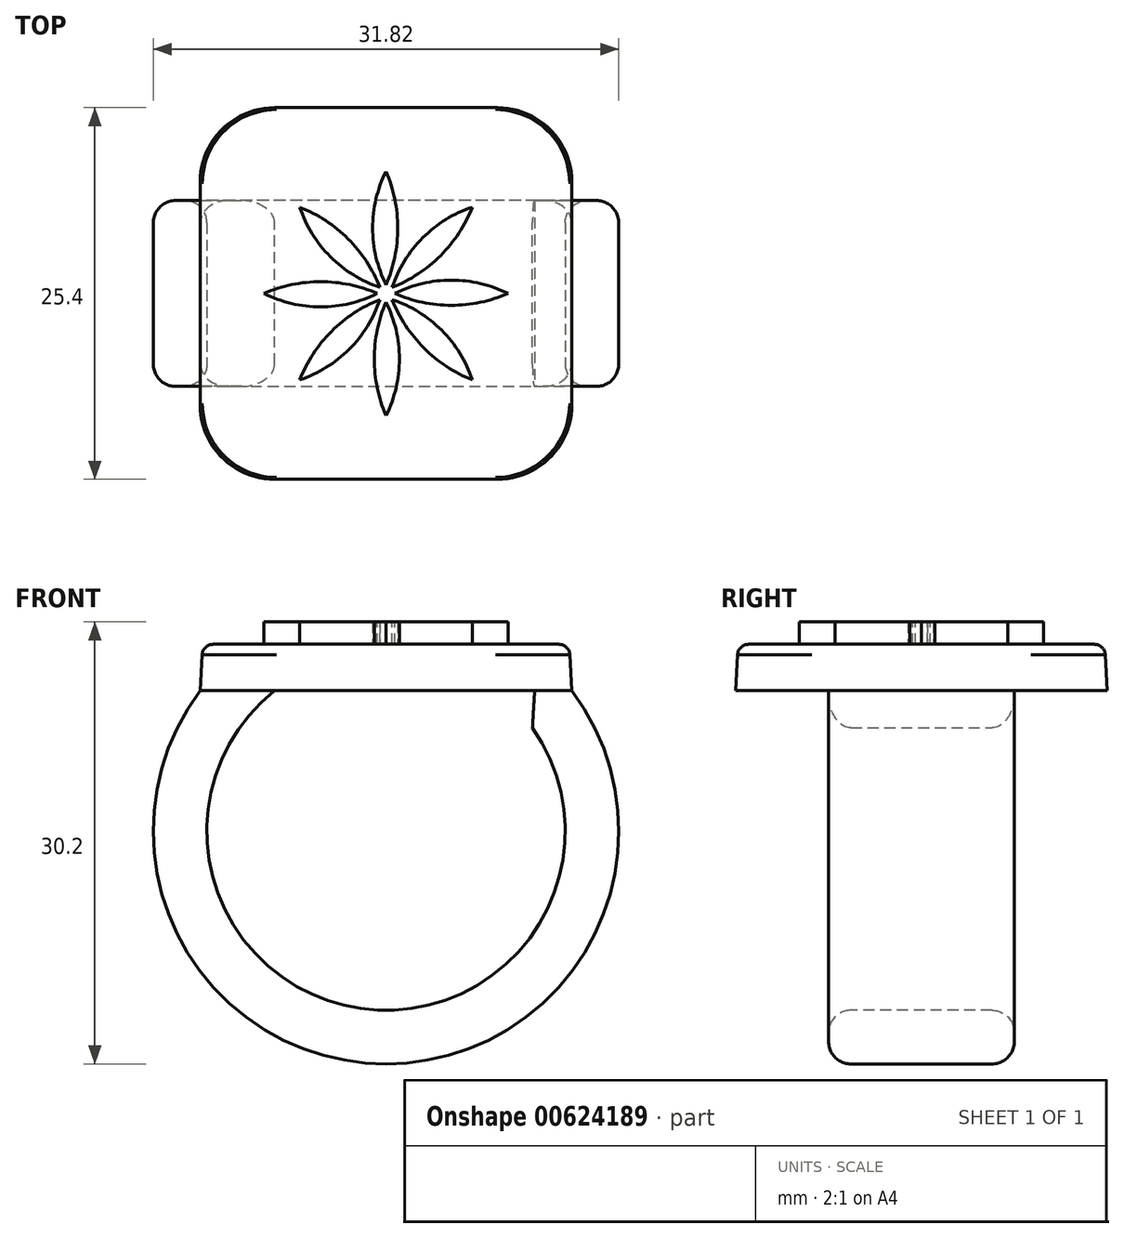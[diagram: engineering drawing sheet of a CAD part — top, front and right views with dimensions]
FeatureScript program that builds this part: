
annotation { "Feature Type Name" : "Feature", "Feature Type Description" : "" }
export const myFeature = defineFeature(function(context is Context, id is Id, definition is map)
    precondition{}
    {
        {
            var Q0;
            Q0=qCreatedBy(makeId("Top.planeOp"),FACE);
            var sketch = newSketch(context, id + "F0", { "sketchPlane" : qUnion([Q0])});
            skLineSegment(sketch, "E0.bottom", {"start": v(12.7, 12.7) * mm, "end": v(-12.7, 12.7) * mm});
            skLineSegment(sketch, "E0.top", {"start": v(12.7, -12.7) * mm, "end": v(-12.7, -12.7) * mm});
            skLineSegment(sketch, "E0.left", {"start": v(12.7, 12.7) * mm, "end": v(12.7, -12.7) * mm});
            skLineSegment(sketch, "E0.right", {"start": v(-12.7, 12.7) * mm, "end": v(-12.7, -12.7) * mm});
            skPoint(sketch, "E0.middle", {"position": v(0, 0) * mm});
            skSolve(sketch);
        }
        {
            var Q0;
            Q0=qSketchRegion(id+"F0",true);
            extrude(context, id + "F1", {"entities" : qUnion([Q0]), "depth" : 3.17 * mm, "hasDraft" : true, "draftAngle" : 3 * degree, "draftPullDirection" : true});
        }
        {
            var Q0;
            Q0=qCreatedBy(makeId("Front.planeOp"),FACE);
            var sketch = newSketch(context, id + "F2", { "sketchPlane" : qUnion([Q0])});
            skArc(sketch, "E1", {"start": v(-10.16, 0) * mm, "mid": v(0, -23.56) * mm, "end": v(10.16, 0) * mm});
            skSolve(sketch);
        }
        {
            var Q0;
            Q0=makeQuery(id+"F1.opExtrude","CAP_FACE",FACE,{"disambiguationData":[OSD([sQuery(id+"F0.wireOp",EDGE,"E0.bottom"),sQuery(id+"F0.wireOp",EDGE,"E0.top"),sQuery(id+"F0.wireOp",EDGE,"E0.left"),sQuery(id+"F0.wireOp",EDGE,"E0.right")])],"isStart":true});
            var sketch = newSketch(context, id + "F3", { "sketchPlane" : qUnion([Q0])});
            skLineSegment(sketch, "E2.bottom", {"start": v(-12.7, 6.35) * mm, "end": v(-7.62, 6.35) * mm});
            skLineSegment(sketch, "E2.top", {"start": v(-12.7, -6.35) * mm, "end": v(-7.62, -6.35) * mm});
            skLineSegment(sketch, "E2.left", {"start": v(-12.7, 6.35) * mm, "end": v(-12.7, -6.35) * mm});
            skLineSegment(sketch, "E2.right", {"start": v(-7.62, 6.35) * mm, "end": v(-7.62, -6.35) * mm});
            skPoint(sketch, "E2.middle", {"position": v(-10.16, 0) * mm});
            skSolve(sketch);
        }
        {
            var Q0;
            Q0=qSketchRegion(id+"F3",true);
            var Q1;
            Q1=qConstructionFilter(qBodyType(qCreatedBy(id+"F2",EDGE),BodyType.WIRE),ConstructionObject.NO);
            sweep(context, id + "F4", {"operationType" : NewBodyOperationType.ADD, "profiles" : qUnion([Q0]), "path" : qUnion([Q1])});
        }
        {
            var Q0;
            Q0=qCreatedBy(makeId("Front.planeOp"),FACE);
            var sketch = newSketch(context, id + "F5", { "sketchPlane" : qUnion([Q0])});
            skLineSegment(sketch, "E3.1", {"start": v(10.01, -2.54) * mm, "end": v(10.16, 0) * mm});
            skArc(sketch, "E3.2", {"start": v(10.01, -2.54) * mm, "mid": v(8.9, -1.18) * mm, "end": v(7.62, 0) * mm});
            skPoint(sketch, "E3.0.1.end.orphan", {"position": v(12.53, 3.18) * mm});
            skPoint(sketch, "E4.orphan", {"position": v(12.7, 0) * mm});
            skLineSegment(sketch, "E5.trimOffspring", {"start": v(7.62, 0) * mm, "end": v(10.16, 0) * mm});
            skPoint(sketch, "E3.0.3.start.orphan", {"position": v(-12.53, 3.18) * mm});
            skPoint(sketch, "E3.0.0.start.orphan", {"position": v(-12.7, 0) * mm});
            skPoint(sketch, "E6.orphan", {"position": v(-7.62, 0) * mm});
            skSolve(sketch);
        }
        {
            var Q0;
            Q0=makeQuery(id+"F1.opExtrude","SWEPT_EDGE",EDGE,{"disambiguationData":[OSD([sQuery(id+"F0.wireOp",EDGE,"E0.bottom"),sQuery(id+"F0.wireOp",EDGE,"E0.right")])]});
            var Q1;
            Q1=makeQuery(id+"F1.opExtrude","SWEPT_EDGE",EDGE,{"disambiguationData":[OSD([sQuery(id+"F0.wireOp",EDGE,"E0.top"),sQuery(id+"F0.wireOp",EDGE,"E0.right")])]});
            var Q2;
            Q2=makeQuery(id+"F1.opExtrude","SWEPT_EDGE",EDGE,{"disambiguationData":[OSD([sQuery(id+"F0.wireOp",EDGE,"E0.top"),sQuery(id+"F0.wireOp",EDGE,"E0.left")])]});
            var Q3;
            Q3=makeQuery(id+"F1.opExtrude","SWEPT_EDGE",EDGE,{"disambiguationData":[OSD([sQuery(id+"F0.wireOp",EDGE,"E0.bottom"),sQuery(id+"F0.wireOp",EDGE,"E0.left")])]});
            fillet(context, id + "F6", {"entities" : qUnion([Q0, Q1, Q2, Q3]), "radius" : 5.08 * mm, "tangentPropagation" : true, "allowEdgeOverflow" : false});
        }
        {
            var Q0;
            {var subQ0=sQuery(id+"F3.wireOp",EDGE,"E2.bottom");var subQ1=sQuery(id+"F2.wireOp",EDGE,"E1");Q0=makeQuery(id+"F6jFjd80Wf5al8X_1.boolean.opBoolean","MERGE",EDGE,{"derivedFrom":[makeQuery(id+"F4.opSweep","SWEPT_EDGE",EDGE,{"disambiguationData":[OSD([subQ1,subQ0,sQuery(id+"F3.wireOp",EDGE,"E2.right")])]}),makeQuery(id+"F6jFjd80Wf5al8X_1.opExtrude","TWEAK_EDGE",EDGE,{"derivedFrom":[makeQuery(id+"F4.opSweep","SWEPT_FACE",FACE,{"disambiguationData":[OSD([subQ1,subQ0])]}),makeQuery(id+"F5.imprint","IMPRINT",EDGE,{"derivedFrom":sQuery(id+"F5.wireOp",EDGE,"E3.2")})]})]});}
            var Q1;
            {var subQ0=sQuery(id+"F3.wireOp",EDGE,"E2.top");var subQ1=sQuery(id+"F2.wireOp",EDGE,"E1");Q1=makeQuery(id+"F6jFjd80Wf5al8X_1.boolean.opBoolean","MERGE",EDGE,{"derivedFrom":[makeQuery(id+"F4.opSweep","SWEPT_EDGE",EDGE,{"disambiguationData":[OSD([subQ1,subQ0,sQuery(id+"F3.wireOp",EDGE,"E2.right")])]}),makeQuery(id+"F6jFjd80Wf5al8X_1.opExtrude","TWEAK_EDGE",EDGE,{"derivedFrom":[makeQuery(id+"F4.opSweep","SWEPT_FACE",FACE,{"disambiguationData":[OSD([subQ1,subQ0])]}),makeQuery(id+"F5.imprint","IMPRINT",EDGE,{"derivedFrom":sQuery(id+"F5.wireOp",EDGE,"E3.2")})]})]});}
            var Q2;
            Q2=makeQuery(id+"F4.opSweep","SWEPT_EDGE",EDGE,{"disambiguationData":[OSD([sQuery(id+"F0.wireOp",EDGE,"E0.right"),sQuery(id+"F2.wireOp",EDGE,"E1"),sQuery(id+"F3.wireOp",EDGE,"E2.bottom"),sQuery(id+"F3.wireOp",EDGE,"E2.left")])]});
            var Q3;
            Q3=makeQuery(id+"F4.opSweep","SWEPT_EDGE",EDGE,{"disambiguationData":[OSD([sQuery(id+"F0.wireOp",EDGE,"E0.right"),sQuery(id+"F2.wireOp",EDGE,"E1"),sQuery(id+"F3.wireOp",EDGE,"E2.top"),sQuery(id+"F3.wireOp",EDGE,"E2.left")])]});
            fillet(context, id + "F7", {"entities" : qUnion([Q0, Q1, Q2, Q3]), "radius" : 1.52 * mm, "tangentPropagation" : true, "allowEdgeOverflow" : false});
        }
        {
            var Q0;
            Q0=makeQuery(id+"F1.opExtrude","CAP_FACE",FACE,{"disambiguationData":[OSD([sQuery(id+"F0.wireOp",EDGE,"E0.bottom"),sQuery(id+"F0.wireOp",EDGE,"E0.top"),sQuery(id+"F0.wireOp",EDGE,"E0.left"),sQuery(id+"F0.wireOp",EDGE,"E0.right")])],"isStart":false});
            fillet(context, id + "F8", {"entities" : qUnion([Q0]), "radius" : 0.76 * mm, "tangentPropagation" : true, "allowEdgeOverflow" : false});
        }
        {
            var Q0;
            Q0=makeQuery(id+"F1.opExtrude","CAP_FACE",FACE,{"disambiguationData":[OSD([sQuery(id+"F0.wireOp",EDGE,"E0.bottom"),sQuery(id+"F0.wireOp",EDGE,"E0.top"),sQuery(id+"F0.wireOp",EDGE,"E0.left"),sQuery(id+"F0.wireOp",EDGE,"E0.right")])],"isStart":false});
            var sketch = newSketch(context, id + "F9", { "sketchPlane" : qUnion([Q0])});
            skCircle(sketch, "E7", {"center": v(0, 0) * mm, "radius": 0.6 * mm});
            skArc(sketch, "E8", {"start": v(0, 0.6) * mm, "mid": v(0.6, 2.5) * mm, "end": v(0.8, 4.47) * mm});
            skArc(sketch, "E9", {"start": v(0.8, 4.47) * mm, "mid": v(0.6, 6.45) * mm, "end": v(0, 8.34) * mm});
            skArc(sketch, "E10", {"start": v(0, 8.34) * mm, "mid": v(-0.68, 6.46) * mm, "end": v(-0.92, 4.47) * mm});
            skArc(sketch, "E11", {"start": v(-0.92, 4.47) * mm, "mid": v(-0.68, 2.48) * mm, "end": v(0, 0.6) * mm});
            skArc(sketch, "E12", {"start": v(-0.42, 0.42) * mm, "mid": v(-1.34, 2.19) * mm, "end": v(-2.6, 3.73) * mm});
            skArc(sketch, "E13", {"start": v(-2.6, 3.73) * mm, "mid": v(-4.13, 4.98) * mm, "end": v(-5.9, 5.9) * mm});
            skArc(sketch, "E14", {"start": v(-5.9, 5.9) * mm, "mid": v(-5.05, 4.08) * mm, "end": v(-3.8, 2.51) * mm});
            skArc(sketch, "E15", {"start": v(-3.8, 2.51) * mm, "mid": v(-2.24, 1.27) * mm, "end": v(-0.42, 0.42) * mm});
            skArc(sketch, "E16", {"start": v(-0.6, 0) * mm, "mid": v(-2.5, 0.6) * mm, "end": v(-4.47, 0.8) * mm});
            skArc(sketch, "E17", {"start": v(-4.47, 0.8) * mm, "mid": v(-6.45, 0.6) * mm, "end": v(-8.34, 0) * mm});
            skArc(sketch, "E18", {"start": v(-8.34, 0) * mm, "mid": v(-6.46, -0.68) * mm, "end": v(-4.47, -0.92) * mm});
            skArc(sketch, "E19", {"start": v(-4.47, -0.92) * mm, "mid": v(-2.48, -0.68) * mm, "end": v(-0.6, 0) * mm});
            skArc(sketch, "E20", {"start": v(-0.42, -0.42) * mm, "mid": v(-2.19, -1.34) * mm, "end": v(-3.73, -2.59) * mm});
            skArc(sketch, "E21", {"start": v(-3.73, -2.59) * mm, "mid": v(-4.98, -4.13) * mm, "end": v(-5.9, -5.9) * mm});
            skArc(sketch, "E22", {"start": v(-5.9, -5.9) * mm, "mid": v(-4.08, -5.05) * mm, "end": v(-2.51, -3.8) * mm});
            skArc(sketch, "E23", {"start": v(-2.51, -3.8) * mm, "mid": v(-1.27, -2.24) * mm, "end": v(-0.42, -0.42) * mm});
            skArc(sketch, "E24", {"start": v(0, -0.6) * mm, "mid": v(-0.6, -2.5) * mm, "end": v(-0.8, -4.47) * mm});
            skArc(sketch, "E25", {"start": v(-0.8, -4.47) * mm, "mid": v(-0.6, -6.45) * mm, "end": v(0, -8.34) * mm});
            skArc(sketch, "E26", {"start": v(0, -8.34) * mm, "mid": v(0.68, -6.46) * mm, "end": v(0.92, -4.47) * mm});
            skArc(sketch, "E27", {"start": v(0.92, -4.47) * mm, "mid": v(0.68, -2.48) * mm, "end": v(0, -0.6) * mm});
            skArc(sketch, "E28", {"start": v(0.42, -0.42) * mm, "mid": v(1.34, -2.19) * mm, "end": v(2.59, -3.73) * mm});
            skArc(sketch, "E29", {"start": v(2.59, -3.73) * mm, "mid": v(4.13, -4.98) * mm, "end": v(5.9, -5.9) * mm});
            skArc(sketch, "E30", {"start": v(5.9, -5.9) * mm, "mid": v(5.05, -4.08) * mm, "end": v(3.8, -2.51) * mm});
            skArc(sketch, "E31", {"start": v(3.8, -2.51) * mm, "mid": v(2.24, -1.27) * mm, "end": v(0.42, -0.42) * mm});
            skArc(sketch, "E32", {"start": v(0.6, 0) * mm, "mid": v(2.5, -0.6) * mm, "end": v(4.47, -0.8) * mm});
            skArc(sketch, "E33", {"start": v(4.47, -0.8) * mm, "mid": v(6.45, -0.6) * mm, "end": v(8.34, 0) * mm});
            skArc(sketch, "E34", {"start": v(8.34, 0) * mm, "mid": v(6.46, 0.68) * mm, "end": v(4.47, 0.92) * mm});
            skArc(sketch, "E35", {"start": v(4.47, 0.92) * mm, "mid": v(2.48, 0.68) * mm, "end": v(0.6, 0) * mm});
            skArc(sketch, "E36", {"start": v(0.42, 0.42) * mm, "mid": v(2.19, 1.34) * mm, "end": v(3.73, 2.6) * mm});
            skArc(sketch, "E37", {"start": v(3.73, 2.6) * mm, "mid": v(4.98, 4.13) * mm, "end": v(5.9, 5.9) * mm});
            skArc(sketch, "E38", {"start": v(5.9, 5.9) * mm, "mid": v(4.08, 5.05) * mm, "end": v(2.51, 3.8) * mm});
            skArc(sketch, "E39", {"start": v(2.51, 3.8) * mm, "mid": v(1.27, 2.24) * mm, "end": v(0.42, 0.42) * mm});
            skSolve(sketch);
        }
        {
            var Q0;
            Q0=makeQuery(id+"F9.imprint","IMPRINT",FACE,{"disambiguationData":[TD([[makeQuery(id+"F9.imprint","IMPRINT",EDGE,{"derivedFrom":sQuery(id+"F9.wireOp",EDGE,"E12")}),1.0]])]});
            var Q1;
            Q1=makeQuery(id+"F9.imprint","IMPRINT",FACE,{"disambiguationData":[TD([[makeQuery(id+"F9.imprint","IMPRINT",EDGE,{"derivedFrom":sQuery(id+"F9.wireOp",EDGE,"E8")}),1.0]])]});
            var Q2;
            Q2=makeQuery(id+"F9.imprint","IMPRINT",FACE,{"disambiguationData":[TD([[makeQuery(id+"F9.imprint","IMPRINT",EDGE,{"derivedFrom":sQuery(id+"F9.wireOp",EDGE,"E36")}),1.0]])]});
            var Q3;
            Q3=makeQuery(id+"F9.imprint","IMPRINT",FACE,{"disambiguationData":[TD([[makeQuery(id+"F9.imprint","IMPRINT",EDGE,{"derivedFrom":sQuery(id+"F9.wireOp",EDGE,"E32")}),1.0]])]});
            var Q4;
            Q4=makeQuery(id+"F9.imprint","IMPRINT",FACE,{"disambiguationData":[TD([[makeQuery(id+"F9.imprint","IMPRINT",EDGE,{"derivedFrom":sQuery(id+"F9.wireOp",EDGE,"E28")}),1.0]])]});
            var Q5;
            Q5=makeQuery(id+"F9.imprint","IMPRINT",FACE,{"disambiguationData":[TD([[makeQuery(id+"F9.imprint","IMPRINT",EDGE,{"derivedFrom":sQuery(id+"F9.wireOp",EDGE,"E24")}),1.0]])]});
            var Q6;
            Q6=makeQuery(id+"F9.imprint","IMPRINT",FACE,{"disambiguationData":[TD([[makeQuery(id+"F9.imprint","IMPRINT",EDGE,{"derivedFrom":sQuery(id+"F9.wireOp",EDGE,"E20")}),1.0]])]});
            var Q7;
            Q7=makeQuery(id+"F9.imprint","IMPRINT",FACE,{"disambiguationData":[TD([[makeQuery(id+"F9.imprint","IMPRINT",EDGE,{"derivedFrom":sQuery(id+"F9.wireOp",EDGE,"E16")}),1.0]])]});
            extrude(context, id + "F10", {"entities" : qUnion([Q0, Q1, Q2, Q3, Q4, Q5, Q6, Q7]), "operationType" : NewBodyOperationType.ADD, "depth" : 1.52 * mm, "offsetDistance" : 25.4 * mm});
        }
    });
